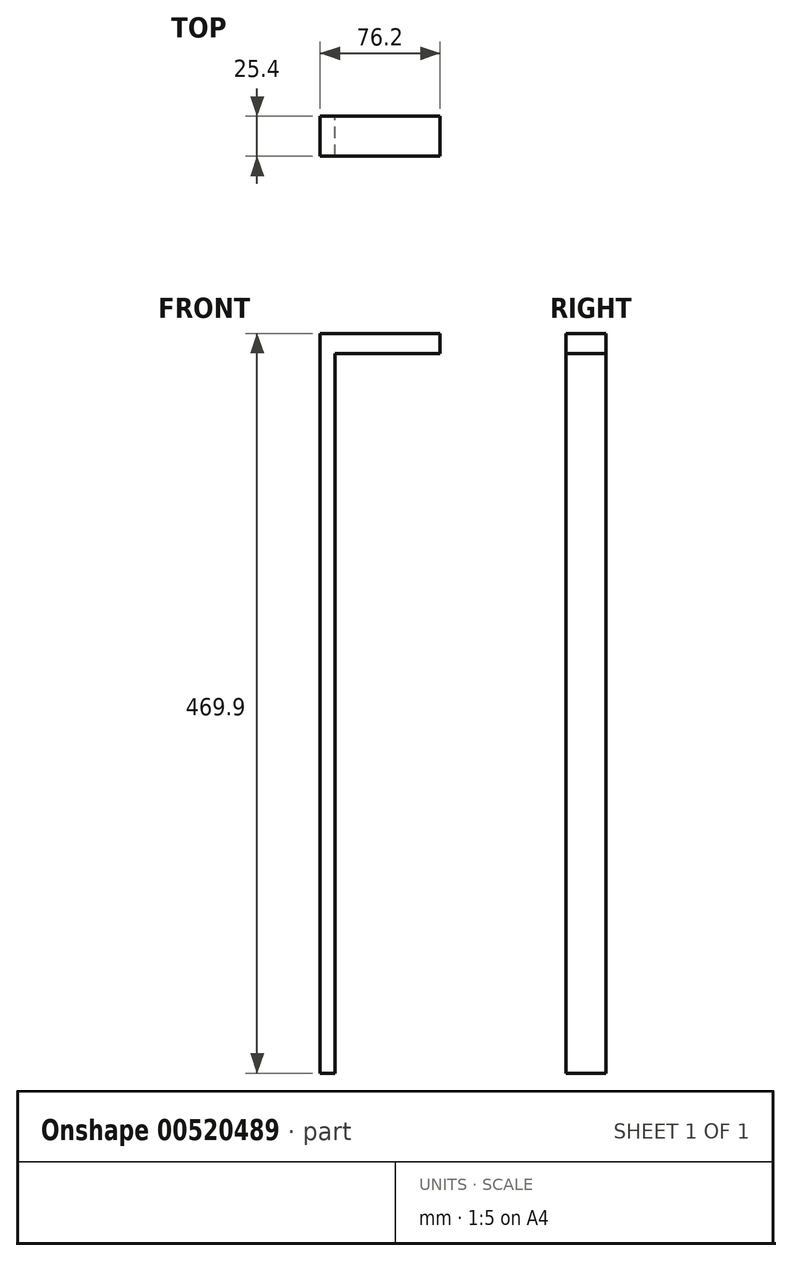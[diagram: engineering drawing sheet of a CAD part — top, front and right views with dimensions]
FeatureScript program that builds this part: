
annotation { "Feature Type Name" : "Feature", "Feature Type Description" : "" }
export const myFeature = defineFeature(function(context is Context, id is Id, definition is map)
    precondition{}
    {
        {
            var Q0;
            Q0=qCreatedBy(makeId("Top.planeOp"),FACE);
            var sketch = newSketch(context, id + "F0", { "sketchPlane" : qUnion([Q0])});
            skLineSegment(sketch, "E0.bottom", {"start": v(-8.86, 19.52) * mm, "end": v(67.34, 19.52) * mm});
            skLineSegment(sketch, "E0.top", {"start": v(-8.86, -5.88) * mm, "end": v(67.34, -5.88) * mm});
            skLineSegment(sketch, "E0.left", {"start": v(-8.86, 19.52) * mm, "end": v(-8.86, -5.88) * mm});
            skLineSegment(sketch, "E0.right", {"start": v(67.34, 19.52) * mm, "end": v(67.34, -5.88) * mm});
            skSolve(sketch);
        }
        {
            var Q0;
            Q0=makeQuery(id+"F0.imprint","IMPRINT",FACE,{"disambiguationData":[TD([[makeQuery(id+"F0.imprint","IMPRINT",EDGE,{"derivedFrom":sQuery(id+"F0.wireOp",EDGE,"E0.bottom")}),-1.0]])]});
            extrude(context, id + "F1", {"entities" : qUnion([Q0]), "depth" : 12.7 * mm, "offsetDistance" : 25.4 * mm});
        }
        {
            var Q0;
            Q0=makeQuery(id+"F1.opExtrude","CAP_FACE",FACE,{"disambiguationData":[OSD([sQuery(id+"F0.wireOp",EDGE,"E0.bottom"),sQuery(id+"F0.wireOp",EDGE,"E0.top"),sQuery(id+"F0.wireOp",EDGE,"E0.left"),sQuery(id+"F0.wireOp",EDGE,"E0.right")])],"isStart":true});
            var sketch = newSketch(context, id + "F2", { "sketchPlane" : qUnion([Q0])});
            skLineSegment(sketch, "E1", {"start": v(-8.86, 5.88) * mm, "end": v(67.34, 5.88) * mm});
            skLineSegment(sketch, "E2", {"start": v(67.34, 5.88) * mm, "end": v(29.24, 5.88) * mm});
            skLineSegment(sketch, "E3", {"start": v(29.24, 5.88) * mm, "end": v(48.3, 5.88) * mm});
            skLineSegment(sketch, "E4", {"start": v(67.34, 5.88) * mm, "end": v(48.3, 5.88) * mm});
            skLineSegment(sketch, "E5", {"start": v(57.82, 5.88) * mm, "end": v(57.82, -19.52) * mm});
            skLineSegment(sketch, "E6", {"start": v(57.82, -19.52) * mm, "end": v(57.82, 4.3) * mm});
            skLineSegment(sketch, "E7", {"start": v(57.82, 4.3) * mm, "end": v(57.82, 5.88) * mm});
            skLineSegment(sketch, "E8", {"start": v(-8.86, 5.88) * mm, "end": v(29.24, 5.88) * mm});
            skLineSegment(sketch, "E9", {"start": v(10.2, 5.88) * mm, "end": v(-8.86, 5.88) * mm});
            skLineSegment(sketch, "E10", {"start": v(0.67, 5.88) * mm, "end": v(0.67, -19.52) * mm});
            skSolve(sketch);
        }
        {
            var Q0;
            Q0 = qSketchRegion(id + "F2", true);
            var Q1;
            {var subQ2=sQuery(id+"F2.wireOp",EDGE,"E10");Q1=makeQuery(id+"F2.imprint","IMPRINT",FACE,{"disambiguationData":[TD([[makeQuery(id+"F2.imprint","IMPRINT",EDGE,{"derivedFrom":subQ2}),-1.0]])]});}
            var Q2;
            {var subQ2=sQuery(id+"F2.wireOp",EDGE,"E6");Q2=makeQuery(id+"F2.imprint","IMPRINT",FACE,{"disambiguationData":[TD([[makeQuery(id+"F2.imprint","IMPRINT",EDGE,{"derivedFrom":subQ2}),-1.0]])]});}
            extrude(context, id + "F3", {"entities" : qUnion([Q0, Q1, Q2]), "operationType" : NewBodyOperationType.ADD, "depth" : 457.2 * mm, "offsetDistance" : 25.4 * mm});
        }
    });
